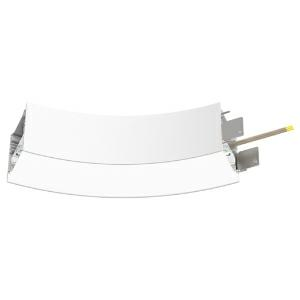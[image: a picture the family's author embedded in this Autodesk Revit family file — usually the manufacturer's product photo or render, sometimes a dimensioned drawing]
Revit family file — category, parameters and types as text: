
# Revit family: super-g_slim_super_g_slim_800_45deg_hl_ps_led__6w_790lm_3000k_cri_80_430-1620_2f74
name_source: partatom
category: Leuchten
revit_build: Autodesk Revit 2016 (Build: 20190508_0715(x64)
units: mm (PartAtom-declared; Revit-internal decimal feet)

## family parameters
Basisbauteil = Fläche
Beim Laden mit Abzugskörper schneiden = Nein
Bemaßung runder Anschluss = Durchmesser verwenden
Gemeinsam genutzt = Nein
Lichtquelle = Nein
Raumberechnungspunkt = Nein
Teiletyp = Normal

## types (1)
- 430-1620-D01 (1 x LED, 480 lm, 3000K)
    Approval mark = CE
    Beschreibung = The insert consists of aluminum-extruded profile. Charming SOFT-EDGE design ensure unparalleled styling. The ballast is integrated and allows for an operation with 220-240V (50/60Hz). SUPER-G SLIM (# 430-1620) ist not dimmable (on/off).
    CIE Flux Codes = 48 79 96 100 71
    Color Rendering = 1B/80…89
    Color Temperature = 3000K
    Height = 90 mm
    Hersteller = Prolicht
    Lamp Light Flux = 480 lm
    Lamp count = 1
    Lampe = 1 x LED
    Length = 144 mm
    Luminous efficacy = 103 lm/W
    ModVariant = Nein
    Modell = 430-1620
    Mounting Place = Ceiling
    Mounting Type = Pendant
    Number of Poles = 1
    OnlyDefault = Ja
    Power Factor = 1
    Product Name = SUPER-G SLIM__SUPER G SLIM 800/45° HL PS LED: 6W 790lm 3000K CRI:80
    Product group = Suspended profile systems
    ProductGroupID = 944
    Protection Class = Protection class I
    Protection Degree = IP 20
    RLX_Detail_Level = 1
    RlxData = <blob elided: 37729 chars, md5=808323f2>
    Scheinlast = 7 VA
    Socket = socket
    Standby Power = 0 W
    System Light Flux = 681 lm
    System Power = 7 W
    Typenbild = 430-1620.jpg
    URL = http://relux.com
    VarID = 430-1620-d01
    Voltage = 0 V
    Vorgabe-Ansicht = 1800 mm
    Weight = 0.00 kg
    Width = 65 mm

## geometry (parser evidence)
native form markers: Sweep x14
no freeform markers — native parametric forms only
